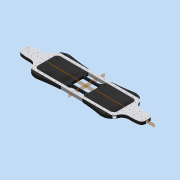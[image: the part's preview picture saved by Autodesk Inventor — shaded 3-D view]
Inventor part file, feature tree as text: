
AUTODESK INVENTOR PART (.ipt)
format: ipt  version: 2015 (Build 190159000, 159)  size: 3,054,592 bytes
history: native  units: in
note: dims shown in document units (in); Inventor stores cm internally (conversion verified against a paired STEP export)
features: sketch x37, projected_geometry x37, extrude x36, other x33, fillet x28, chamfer x10, plane x9, mirror x6, hole x5, shell x3, split x3
ambient origin geometry x2: Origin, Center Point
bodies: Body1 (feature_tree), Body2 (feature_tree), Body3 (feature_tree), Body4 (feature_tree), Body5 (feature_tree), Body6 (feature_tree), Body7 (feature_tree), Body8 (feature_tree), Body9 (feature_tree), Body10 (feature_tree), Body11 (feature_tree), Body12 (feature_tree), Body13 (feature_tree), Body14 (feature_tree), Body15 (feature_tree), Body16 (feature_tree), Body17 (feature_tree)
feature tree (207):
  other  "CrossSection1"
  other  "Curvature1"
  other  "CrossSection2"
  other  "main_support0"
  extrude  "Extrusion1"  Depth=0.75in
  plane  "Work Plane1"
  shell  "Shell2"  Thickness=24.0in
  extrude  "Extrusion33"  Depth=1.5in
  fillet  "Fillet23"  Radius=1.5in
  mirror  "Mirror2"
  extrude  "Extrusion3"  Depth=1.5in TaperAngle=45.0deg
  chamfer  "Chamfer1"  Distance=0.0625in
  fillet  "Fillet3"  Radius=1.0in
  extrude  "Handles"  Depth=0.75in
  fillet  "Fillet4"  Radius=0.0625in
  fillet  "Fillet5"  Radius=0.0625in
  plane  "Work Plane2"
  extrude  "Horiz_ Bar"  Depth=5.5in
  shell  "HorizBar_Shell"  Thickness=0.201in
  mirror  "HorizBar_Mirror"
  extrude  "TopPlate_Extrude"  Depth=0.201in
  fillet  "Fillet10"  Radius=0.201in
  chamfer  "Chamfer3"  Distance=0.125in
  fillet  "Fillet6"  Radius=10.0in
  fillet  "Fillet8"  [1 undecoded]
  mirror  "TopPlate_Mirror"
  extrude  "Extrusion9"  Depth=0.75in
  shell  "Shell5"  Thickness=0.0625in
  mirror  "Mirror6"
  extrude  "BottomPlate_TruckMounting"  Depth=0.125in TaperAngle=45.0deg
  fillet  "Fillet9"  Radius=1.0in
  extrude  "Stanoffs"  Depth=3.0in
  mirror  "Mirror9"
  extrude  "Extrusion16"  Depth=0.5in
  extrude  "Extrusion19"  Depth=0.0625in TaperAngle=0.0deg
  extrude  "Extrusion20"  TaperAngle=0.0deg  [1 undecoded]
  extrude  "Curvypart"  Depth=0.191in
  fillet  "Fillet11"  Radius=1.0in
  extrude  "Extrusion24"  Depth=0.25in
  chamfer  "Chamfer5"  Distance=1.0in
  chamfer  "Chamfer6"  Distance=1.0in
  fillet  "Fillet18"  Radius=1.5in
  extrude  "Handlecutout"  Depth=1.0in TaperAngle=0.0deg
  extrude  "Fins"  Depth=7.0in
  extrude  "Heads"  Depth=1.0in TaperAngle=0.0deg
  mirror  "Mirror13"
  fillet  "Fillet20"  [1 undecoded]
  extrude  "Extrusion28"  Depth=1.0in TaperAngle=0.0deg
  plane  "Work Plane6"
  plane  "Work Plane7"
  extrude  "MountSupport_rivetholes"  Depth=0.5in
  fillet  "Fillet28"  Radius=0.375in
  sketch  "Sketch34"  dims[d107=0.5in d108=0.5in]
  extrude  "Extrusion80"  Depth=0.375in
  fillet  "Fillet80"  Radius=0.5in
  fillet  "Fillet81"  Radius=5.0in
  hole  "Hole3"  [1 undecoded]
  hole  "Hole4"  [1 undecoded]
  extrude  "battery cuout"  Depth=0.0787in
  fillet  "Fillet58"  Radius=0.5in
  extrude  "Extrusion63"  Depth=1.0in
  extrude  "Extrusion64"  Depth=1.0in
  extrude  "Extrusion65"  Depth=1.0in
  extrude  "bbox_extrude"  Depth=3.0in
  extrude  "Extrusion67"  Depth=3.0in
  chamfer  "Chamfer19"  Distance=0.013in
  fillet  "Fillet59"  Radius=5.9449in
  chamfer  "Chamfer20"  Distance=2.0866in
  fillet  "Fillet60"  Radius=5.9449in
  chamfer  "Chamfer21"  Distance=0.3937in
  fillet  "Fillet61"  Radius=0.0787in
  chamfer  "Chamfer22"  Distance=2.0866in
  fillet  "Fillet62"  Radius=0.25in
  chamfer  "Chamfer23"  Distance=0.25in
  fillet  "Fillet63"  Radius=4.125in
  fillet  "Fillet65"  Radius=0.4331in
  fillet  "Fillet69"  Radius=0.0938in
  extrude  "Extrusion69"  Depth=1.0in TaperAngle=0.0deg
  chamfer  "Chamfer25"  Distance=0.5in
  fillet  "Fillet83"  Radius=0.375in
  plane  "Work Plane10"
  hole  "Hole5"  [1 undecoded]
  split  "Split2"
  plane  "Work Plane9"
  extrude  "counterbore"  Depth=1.0in
  extrude  "main rivets"  Depth=1.0in
  extrude  "electronics_recess"  Depth=1.0in
  fillet  "Fillet82"  Radius=0.25in
  extrude  "electronics_plate"  Depth=1.0in TaperAngle=0.0deg
  sketch  "Sketch85"  dims[d210=2.3622in d212=1.125in d213=0.3937in d215=1.0in d217=0.375in]
  hole  "Hole6"  [1 undecoded]
  hole  "Hole7"  [1 undecoded]
  extrude  "Extrusion87"  Depth=1.0in
  fillet  "Fillet89"  Radius=0.125in
  fillet  "Fillet90"  Radius=0.5in
  extrude  "Extrusion88"  Depth=0.125in TaperAngle=45.0deg
  fillet  "Fillet91"  Radius=10.0in
  fillet  "Fillet92"  Radius=0.125in
  extrude  "Extrusion89"  Depth=10.0in
  sketch  "Sketch96"  dims[d298=0.3937in d299=0.0in d300=0.25in]
  split  "Split3"
  split  "Split4"
  extrude  "Extrusion90"  Depth=0.125in TaperAngle=45.0deg
  extrude  "Extrusion91"  Depth=1.0in
  plane  "YZ Plane Vertical Spine"
  plane  "XZ Plane Horizontal"
  plane  "XY Plane Vertical Span"
  other  "X Axis Left/Right"
  other  "Y Axis Up/Down"
  other  "Z Axis Fore/Aft"
  sketch  "Sketch1"  dims[d0=0.75in d1=0.75in d2=24.0in d3=0.0in]
  other  "Pattern of main_support0:1"
  other  "main_support1"
  sketch  "Sketch3"  dims[d5=3.25in d6=0.125in d13=1.5in d14=1.5in]
  projected_geometry  "Projected Loop1"
  projected_geometry  "Projected Loop2"
  other  "bottom_plate"
  sketch  "Sketch4"  dims[d16=0.0in d17=1.5in d18=0.125in d19=45.0deg]
  projected_geometry  "Projected Loop3"
  projected_geometry  "Projected Loop4"
  sketch  "Sketch5"  dims[d20=4.0in]
  other  "horiz_support0"
  sketch  "Sketch6"  dims[d22=1.25in]
  other  "TopPlate_0"
  other  "TopPlate_1"
  other  "Pattern of horiz_support0:3"
  other  "horiz_support1"
  sketch  "Sketch9"  dims[d23=6.0in]
  other  "MountSupport_0"
  sketch  "Sketch10"  dims[d24=6.0in d29=0.0625in d30=0.0in d31=1.0in]
  projected_geometry  "Projected Loop10"
  projected_geometry  "Projected Loop11"
  projected_geometry  "Projected Loop12"
  other  "Pattern of horiz_support0:4"
  other  "MountSupport_1"
  sketch  "Sketch15"  dims[d32=1.0in d33=0.75in d35=0.0625in d36=0.0in d37=0.0625in]
  projected_geometry  "Projected Loop20"
  other  "MountStandoffs"
  sketch  "Sketch16"  dims[d41=3.5in d42=5.5in d43=0.201in]
  projected_geometry  "Projected Loop21"
  sketch  "Sketch19"  dims[d44=0.201in d45=0.201in d46=0.201in]
  other  "Printed_Platform"
  sketch  "Sketch21"  dims[d48=1.625in]
  sketch  "Sketch23"  dims[d49=2.5in]
  projected_geometry  "Projected Loop28"
  sketch  "Sketch24"  dims[d50=0.5in d51=0.125in d52=0.0in d53=2.0in d54=10.0in d62=0.0in d63=0.0in]
  projected_geometry  "Projected Loop29"
  other  "Printed_Fins"
  sketch  "Sketch26"  dims[d64=0.0625in d65=0.75in d66=0.0625in d67=0.0in]
  projected_geometry  "Projected Loop36"
  projected_geometry  "Projected Loop37"
  other  "Printed_Heads"
  other  "Printed_Corners"
  sketch  "Sketch27"  dims[d73=5.0in d92=0.375in d93=0.125in d94=45.0deg d95=1.0in]
  projected_geometry  "Projected Loop38"
  sketch  "Sketch31"  dims[d96=3.0in d106=0.5in]
  projected_geometry  "Projected Loop40"
  sketch  "Sketch62"  dims[d109=0.5in d110=0.0625in d111=0.0in]
  sketch  "Sketch63"  dims[d113=1.0in d114=0.0in d115=0.0in]
  projected_geometry  "Projected Loop56"
  sketch  "Sketch64"  dims[d155=0.191in d156=0.191in]
  projected_geometry  "Projected Loop57"
  projected_geometry  "Projected Loop58"
  other  "battery_plate"
  sketch  "Sketch65"  dims[d157=1.1811in d159=1.25in d160=1.1811in d162=1.25in d165=1.0in d166=0.0in]
  projected_geometry  "Projected Loop59"
  projected_geometry  "Projected Loop60"
  other  "battery"
  sketch  "Sketch66"  dims[d167=1.0in d168=0.0in d169=0.25in]
  projected_geometry  "Projected Loop61"
  projected_geometry  "Projected Loop62"
  other  "batterybox"
  sketch  "Sketch67"  dims[d170=0.25in]
  projected_geometry  "Projected Loop63"
  sketch  "Sketch69"  dims[d171=18.0in d172=1.0in d173=0.0in]
  projected_geometry  "Projected Loop64"
  sketch  "Sketch72"  dims[d174=1.0in d182=1.0in d183=0.0in d184=1.5in]
  projected_geometry  "Projected Loop66"
  projected_geometry  "Projected Loop67"
  sketch  "Sketch80"  dims[d185=1.5in d186=1.0in d187=0.0in]
  sketch  "Sketch81"  dims[d190=0.275in d191=1.375in d192=45.0deg d194=7.0in]
  sketch  "Sketch82"  dims[d195=0.275in d196=1.375in d197=45.0deg d198=1.0in d199=0.0in d203=0.0in d204=0.0in]
  projected_geometry  "Projected Loop79"
  sketch  "Sketch83"  dims[d205=1.0in d206=1.0in d207=0.0in]
  projected_geometry  "Projected Loop80"
  sketch  "Sketch84"  dims[d208=0.191in d209=0.5in]
  other  "ebox_plate"
  sketch  "Sketch90"  dims[d218=0.191in d219=0.375in d220=0.5in]
  projected_geometry  "Projected Loop86"
  projected_geometry  "Projected Loop87"
  sketch  "Sketch91"  dims[d221=2.3622in d223=1.125in d224=0.3937in d226=1.0in d228=5.0in d229=0.0in]
  projected_geometry  "Projected Loop88"
  sketch  "Sketch92"  dims[d296=0.75in d297=0.75in]
  projected_geometry  "Projected Loop92"
  projected_geometry  "Projected Loop93"
  projected_geometry  "Projected Loop94"
  sketch  "Sketch97"  dims[d301=0.0in d319=0.0787in d348=0.5in]
  projected_geometry  "Projected Loop95"
  sketch  "Sketch98"  dims[d349=0.201in d350=0.75in d351=0.375in d352=0.25in d353=0.5635in d354=1.0in d355=0.8108in d356=0.159in d357=0.75in d358=0.375in d359=0.313in d360=0.5635in d361=1.0in d362=0.8108in d520=2.0in d522=2.5in d523=2.5in d547=3.0in d548=3.0in d561=0.013in d562=0.5in d563=5.688in d564=2.0in d565=5.9449in d566=2.0866in d567=5.9449in d570=0.3937in d571=0.0in d572=0.0787in d573=2.0866in d574=0.25in d575=0.25in d576=4.125in d577=0.4331in d578=0.0in d579=0.0938in d580=0.0in d581=1.1024in d582=0.0in d583=0.5in d584=0.375in d585=0.375in d586=1.25in d587=1.0in d588=1.0in d589=0.25in d590=0.9843in d591=0.0in d592=0.1875in d593=0.0in d594=0.375in d595=0.125in d596=45.0deg d597=12.0in d598=0.5in d599=0.125in d600=45.0deg d601=0.5in d602=0.125in d603=0.125in d604=45.0deg d605=10.0in d606=0.125in d607=0.125in d608=45.0deg d609=10.0in d610=0.5in d611=0.125in d612=45.0deg d613=1.0in d615=0.125in d626=0.5in d627=0.201in d628=0.201in d629=0.201in d630=0.201in d631=0.75in d632=1.5in d633=0.0312in d634=0.0in d642=0.159in d643=0.75in d644=0.375in d645=0.25in d646=0.5635in d647=1.0in d648=0.8108in d671=0.013in d672=0.5in d673=0.0in d674=2.0in d691=0.25in d692=0.25in d693=10.0861in d694=0.6562in d695=0.375in d696=0.375in d697=0.375in d698=0.375in d699=1.0in d700=0.0in d701=0.191in d702=0.191in d703=1.0in d704=0.0in d705=3.937in d707=1.625in d708=3.937in d710=1.625in d713=1.0in d714=1.0in d715=0.5938in d716=0.0in d717=8.0in d718=5.0in d719=0.25in d720=0.25in d721=2.5in d722=2.5in d723=0.7in d724=0.0in d725=0.0938in d726=0.0in d727=0.25in d728=0.159in d729=0.75in d730=0.375in d731=0.25in d732=0.5635in d733=1.0in d734=0.8108in d735=0.201in d736=0.75in d737=0.375in d738=0.25in d739=0.5635in d740=1.0in d741=0.8108in d750=0.25in d751=0.125in d752=45.0deg d753=1.0in d767=0.5in d768=0.5in d769=0.125in d770=0.0in d771=0.1875in d772=0.25in d773=0.5in d774=0.25in d775=1.0in d779=0.125in d780=0.0938in d781=0.125in d782=0.0938in d783=0.25in d784=0.25in d785=0.0in d786=0.0in d787=2.0in d788=0.5in d789=1.0in d790=0.0in d791=8.125in d792=-0.2061in d794=2.495in d795=2.495in d796=0.5in d797=0.5in d798=1.0in d799=0.0in d800=1.0in d801=0.0in d802=0.201in d803=0.201in d804=0.201in d805=0.201in d806=0.201in d807=0.201in d341=1.0in d342=1.0in]
  projected_geometry  "Projected Loop96"
  projected_geometry  "Projected Loop97"
  other  "batterybox_front"
  other  "bbox_back"
  other  "box_front"
  other  "foot0"
  other  "foot1"
  other  "e_center"
note: 8 required parameter values undecoded (feature->parameter linkage not recoverable at this tier; creation-order binding heuristic only, values carry confidence <= 0.55)
